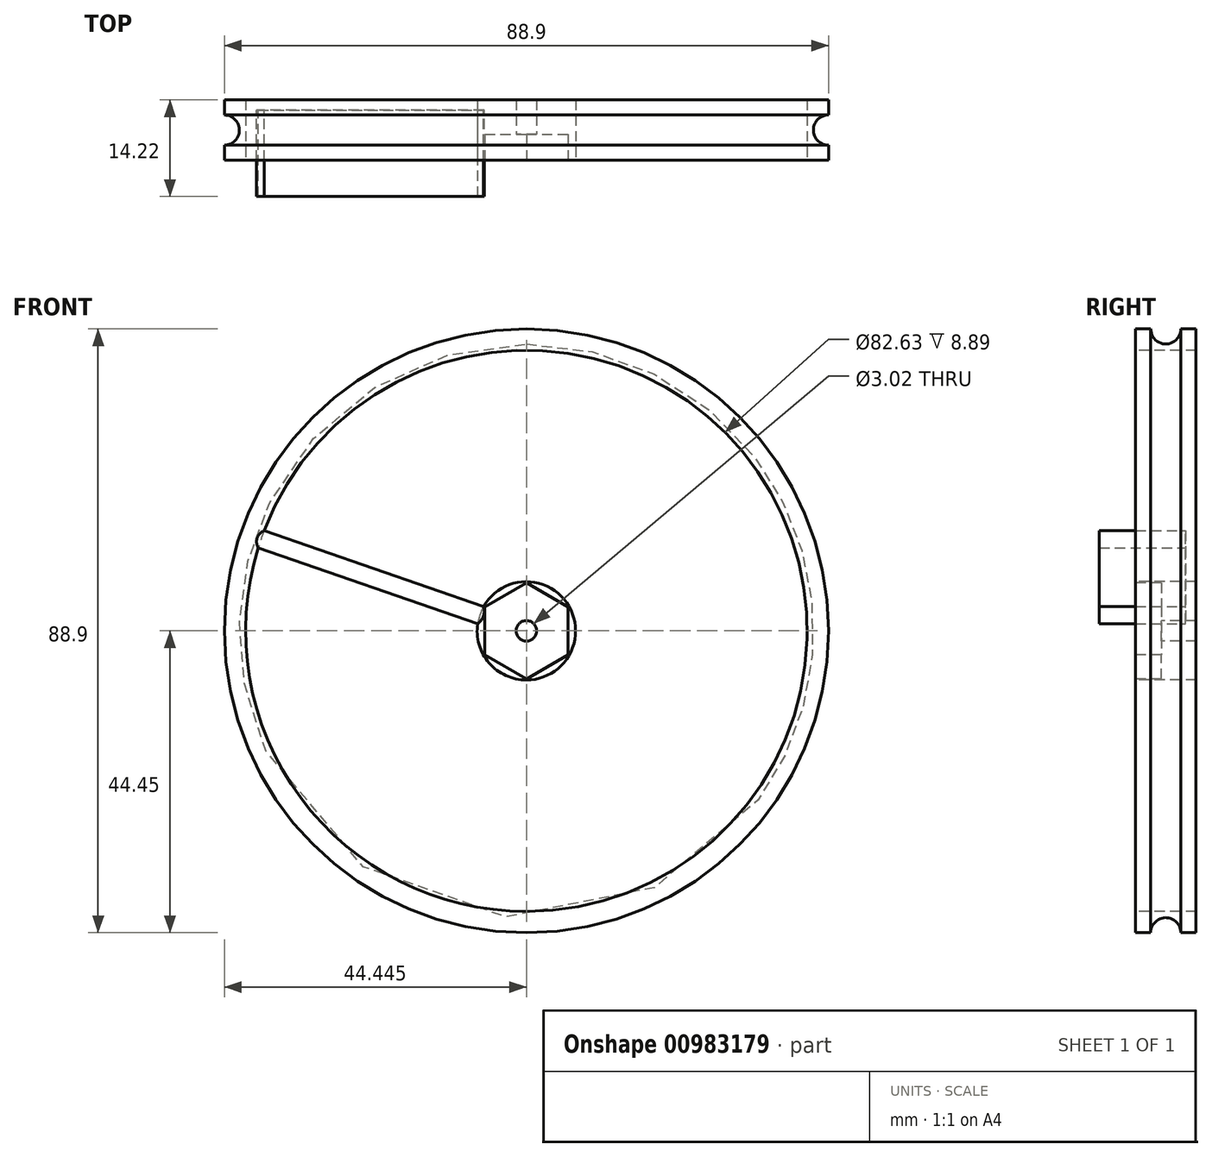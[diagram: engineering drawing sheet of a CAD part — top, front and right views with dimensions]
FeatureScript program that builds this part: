
annotation { "Feature Type Name" : "Feature", "Feature Type Description" : "" }
export const myFeature = defineFeature(function(context is Context, id is Id, definition is map)
    precondition{}
    {
        {
            var Q0;
            Q0=qCreatedBy(makeId("Top.planeOp"),FACE);
            var sketch = newSketch(context, id + "F0", { "sketchPlane" : qUnion([Q0])});
            skLineSegment(sketch, "E0", {"start": v(-7.21, 1.52) * mm, "end": v(37.24, 1.52) * mm});
            skLineSegment(sketch, "E1", {"start": v(-7.21, -7.37) * mm, "end": v(37.24, -7.37) * mm});
            skLineSegment(sketch, "E2", {"start": v(-7.21, 1.52) * mm, "end": v(-7.21, -7.37) * mm});
            skLineSegment(sketch, "E3", {"start": v(37.24, 1.52) * mm, "end": v(37.24, -0.7) * mm});
            skArc(sketch, "E4", {"start": v(37.24, -0.7) * mm, "mid": v(35.01, -2.92) * mm, "end": v(37.24, -5.14) * mm});
            skLineSegment(sketch, "E5.trimOffspring", {"start": v(37.24, -5.14) * mm, "end": v(37.24, -7.37) * mm});
            skLineSegment(sketch, "E6.bottom", {"start": v(-7.21, -7.37) * mm, "end": v(30.89, -7.37) * mm});
            skLineSegment(sketch, "E6.top", {"start": v(-7.21, 1.52) * mm, "end": v(30.89, 1.52) * mm});
            skLineSegment(sketch, "E6.left", {"start": v(-7.21, -7.37) * mm, "end": v(-7.21, 1.52) * mm});
            skLineSegment(sketch, "E6.right", {"start": v(30.89, -7.37) * mm, "end": v(30.89, 1.52) * mm});
            skLineSegment(sketch, "E7.bottom", {"start": v(-7.21, 1.52) * mm, "end": v(1.42, 1.52) * mm});
            skLineSegment(sketch, "E7.top", {"start": v(-7.21, -7.37) * mm, "end": v(1.42, -7.37) * mm});
            skSolve(sketch);
        }
        {
            var Q0;
            {var subQ3=sQuery(id+"F0.wireOp",EDGE,"E3");Q0=makeQuery(id+"F0.imprint","IMPRINT",FACE,{"disambiguationData":[TD([[makeQuery(id+"F0.imprint","IMPRINT",EDGE,{"derivedFrom":subQ3}),-1.0]])]});}
            var Q1;
            {var subQ2=sQuery(id+"F0.wireOp",EDGE,"E2");Q1=makeQuery(id+"F0.imprint","IMPRINT",FACE,{"disambiguationData":[TD([[makeQuery(id+"F0.imprint","IMPRINT",EDGE,{"derivedFrom":subQ2}),1.0]])]});}
            var Q2;
            Q2=sQuery(id+"F0.wireOp",EDGE,"E2");
            revolve(context, id + "F1", {"surfaceOperationType" : NewSurfaceOperationType.NEW, "entities" : qUnion([Q0, Q1]), "axis" : qUnion([Q2]), "revolveType" : RevolveType.FULL});
        }
        {
            var Q0;
            Q0=makeQuery(id+"F1.opRevolve","SWEPT_FACE",FACE,{"disambiguationData":[OSD([sQuery(id+"F0.wireOp",EDGE,"E1")])]});
            var sketch = newSketch(context, id + "F2", { "sketchPlane" : qUnion([Q0])});
            skCircle(sketch, "E8.cCircle", {"center": v(-7.21, 0) * mm, "radius": 6.12 * mm, "construction": true});
            skLineSegment(sketch, "E8.0", {"start": v(-1.1, 3.53) * mm, "end": v(-1.1, -3.53) * mm});
            skLineSegment(sketch, "E8.1", {"start": v(-1.1, -3.53) * mm, "end": v(-7.21, -7.07) * mm});
            skLineSegment(sketch, "E8.2", {"start": v(-7.21, -7.07) * mm, "end": v(-13.34, -3.53) * mm});
            skLineSegment(sketch, "E8.3", {"start": v(-13.34, -3.53) * mm, "end": v(-13.34, 3.53) * mm});
            skLineSegment(sketch, "E8.4", {"start": v(-13.34, 3.53) * mm, "end": v(-7.21, 7.07) * mm});
            skLineSegment(sketch, "E8.5", {"start": v(-7.21, 7.07) * mm, "end": v(-1.1, 3.53) * mm});
            skPoint(sketch, "E8.0.midPoint", {"position": v(-1.1, 0) * mm});
            skCircle(sketch, "E9", {"center": v(-7.21, 0) * mm, "radius": 1.51 * mm});
            skCircle(sketch, "E10", {"center": v(-7.21, 0) * mm, "radius": 7.24 * mm});
            skCircle(sketch, "E11", {"center": v(-7.21, 0) * mm, "radius": 41.32 * mm});
            skSolve(sketch);
        }
        {
            var Q0;
            Q0=makeQuery(id+"F2.imprint","IMPRINT",FACE,{"disambiguationData":[TD([[makeQuery(id+"F2.imprint","IMPRINT",EDGE,{"derivedFrom":sQuery(id+"F2.wireOp",EDGE,"E10")}),-1.0]])]});
            extrude(context, id + "F3", {"entities" : qUnion([Q0]), "operationType" : NewBodyOperationType.REMOVE, "oppositeDirection" : true, "depth" : 25.4 * mm, "offsetDistance" : 25.4 * mm});
        }
        {
            var Q0;
            Q0=makeQuery(id+"F2.imprint","IMPRINT",FACE,{"disambiguationData":[TD([[makeQuery(id+"F2.imprint","IMPRINT",EDGE,{"derivedFrom":sQuery(id+"F2.wireOp",EDGE,"E8.0")}),-1.0]])]});
            extrude(context, id + "F4", {"entities" : qUnion([Q0]), "operationType" : NewBodyOperationType.REMOVE, "oppositeDirection" : true, "depth" : 3.8 * mm, "offsetDistance" : 25.4 * mm});
        }
        {
            var Q0;
            Q0=makeQuery(id+"F2.imprint","IMPRINT",FACE,{"disambiguationData":[TD([[makeQuery(id+"F2.imprint","IMPRINT",EDGE,{"derivedFrom":sQuery(id+"F2.wireOp",EDGE,"E9")}),1.0]])]});
            extrude(context, id + "F5", {"entities" : qUnion([Q0]), "operationType" : NewBodyOperationType.REMOVE, "oppositeDirection" : true, "depth" : 127 * mm, "offsetDistance" : 25.4 * mm});
        }
        {
            var Q0;
            Q0=qCreatedBy(makeId("Front.planeOp"),FACE);
            var sketch = newSketch(context, id + "F6", { "sketchPlane" : qUnion([Q0])});
            skLineSegment(sketch, "E12", {"start": v(-13.5, 3.58) * mm, "end": v(-45.8, 14.75) * mm});
            skLineSegment(sketch, "E13", {"start": v(-46.68, 12.24) * mm, "end": v(-14.37, 1.07) * mm});
            skArc(sketch, "E14", {"start": v(-45.8, 14.75) * mm, "mid": v(-46.82, 13.7) * mm, "end": v(-46.68, 12.24) * mm});
            skArc(sketch, "E15", {"start": v(-14.37, 1.07) * mm, "mid": v(-13.53, 2.18) * mm, "end": v(-13.5, 3.58) * mm});
            skSolve(sketch);
        }
        {
            var Q0;
            Q0=makeQuery(id+"F6.imprint","IMPRINT",FACE,{"disambiguationData":[TD([[makeQuery(id+"F6.imprint","IMPRINT",EDGE,{"derivedFrom":sQuery(id+"F6.wireOp",EDGE,"E12")}),1.0]])]});
            var Q1;
            Q1=sQuery(id+"F6.wireOp",EDGE,"E13");
            var Q2;
            Q2=sQuery(id+"F6.wireOp",EDGE,"E12");
            var Q3;
            Q3=sQuery(id+"F6.wireOp",EDGE,"v3Al41QD-I5n7-ytjn-MVBf-2LGTvXKxpz3j");
            var Q4;
            Q4=sQuery(id+"F6.wireOp",EDGE,"a0UI7Ohi-g6wq-cuqX-wgTp-cieVdNNcMcoD");
            extrude(context, id + "F7", {"entities" : qUnion([Q0]), "surfaceEntities" : qUnion([Q1, Q2, Q3, Q4]), "depth" : 12.7 * mm, "offsetDistance" : 25.4 * mm});
        }
    });
